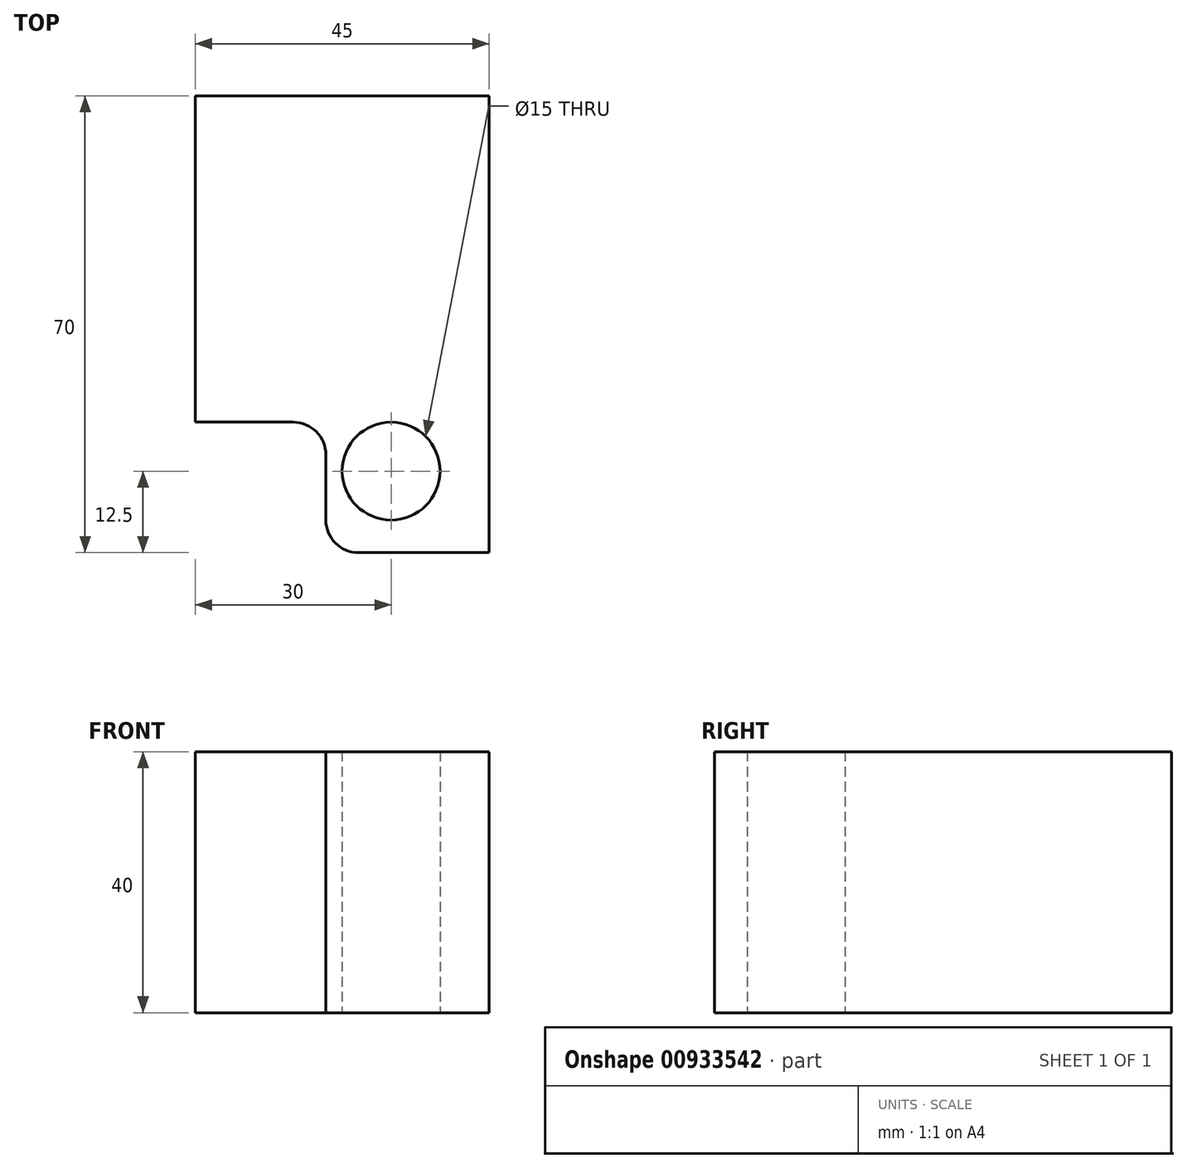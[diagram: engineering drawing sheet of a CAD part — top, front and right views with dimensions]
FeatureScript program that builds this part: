
annotation { "Feature Type Name" : "Feature", "Feature Type Description" : "" }
export const myFeature = defineFeature(function(context is Context, id is Id, definition is map)
    precondition{}
    {
        {
            var Q0;
            Q0=qCreatedBy(makeId("Top.planeOp"),FACE);
            var sketch = newSketch(context, id + "F0", { "sketchPlane" : qUnion([Q0])});
            skLineSegment(sketch, "E0.bottom", {"start": v(0, 0) * mm, "end": v(40, 0) * mm});
            skLineSegment(sketch, "E0.top", {"start": v(0, -5) * mm, "end": v(15, -5) * mm});
            skLineSegment(sketch, "E0.left", {"start": v(0, 0) * mm, "end": v(0, -5) * mm});
            skLineSegment(sketch, "E0.right", {"start": v(40, 0) * mm, "end": v(40, -5) * mm});
            skLineSegment(sketch, "E1", {"start": v(40, 0) * mm, "end": v(40, -12.5) * mm, "construction": true});
            skLineSegment(sketch, "E2", {"start": v(40, -12.5) * mm, "end": v(30, -12.5) * mm, "construction": true});
            skCircle(sketch, "E3", {"center": v(30, -12.5) * mm, "radius": 7.5 * mm});
            skLineSegment(sketch, "E4.top", {"start": v(35, -25) * mm, "end": v(25, -25) * mm});
            skLineSegment(sketch, "E4.right", {"start": v(20, -10) * mm, "end": v(20, -20) * mm});
            skPoint(sketch, "E5.visualSharp", {"position": v(40, -25) * mm});
            skPoint(sketch, "E6.visualSharp", {"position": v(20, -25) * mm});
            skArc(sketch, "E6.filletArc", {"start": v(20, -20) * mm, "mid": v(21.46, -23.54) * mm, "end": v(25, -25) * mm});
            skArc(sketch, "E7.filletArc", {"start": v(20, -10) * mm, "mid": v(18.54, -6.46) * mm, "end": v(15, -5) * mm});
            skLineSegment(sketch, "E8.bottom", {"start": v(40, 0) * mm, "end": v(45, 0) * mm});
            skLineSegment(sketch, "E8.right", {"start": v(45, 0) * mm, "end": v(45, -19.16) * mm});
            skLineSegment(sketch, "E9.bottom", {"start": v(0, 0) * mm, "end": v(45, 0) * mm});
            skLineSegment(sketch, "E9.top", {"start": v(0, 45) * mm, "end": v(45, 45) * mm});
            skLineSegment(sketch, "E9.left", {"start": v(0, 0) * mm, "end": v(0, 45) * mm});
            skLineSegment(sketch, "E9.right", {"start": v(45, 0) * mm, "end": v(45, 45) * mm});
            skLineSegment(sketch, "E10", {"start": v(35, -25) * mm, "end": v(45, -25) * mm});
            skLineSegment(sketch, "E11", {"start": v(45, -25) * mm, "end": v(45, -19.16) * mm});
            skLineSegment(sketch, "E12", {"start": v(30, -12.5) * mm, "end": v(45, -12.5) * mm, "construction": true});
            skSolve(sketch);
        }
        {
            var Q0;
            Q0=makeQuery(id+"F0.imprint","IMPRINT",FACE,{"disambiguationData":[TD([[makeQuery(id+"F0.imprint","IMPRINT",EDGE,{"derivedFrom":sQuery(id+"F0.wireOp",EDGE,"E0.bottom")}),-1.0]])]});
            var Q1;
            Q1=makeQuery(id+"F0.imprint","IMPRINT",FACE,{"disambiguationData":[TD([[makeQuery(id+"F0.imprint","IMPRINT",EDGE,{"derivedFrom":sQuery(id+"F0.wireOp",EDGE,"E0.bottom")}),1.0]])]});
            var Q2;
            Q2=makeQuery(id+"F0.imprint","IMPRINT",FACE,{"disambiguationData":[TD([[makeQuery(id+"F0.imprint","IMPRINT",EDGE,{"derivedFrom":sQuery(id+"F0.wireOp",EDGE,"E0.bottom")}),-1.0]])]});
            var Q3;
            {var subQ3=sQuery(id+"F0.wireOp",EDGE,"E8.top");Q3=makeQuery(id+"F0.imprint","IMPRINT",FACE,{"disambiguationData":[TD([[makeQuery(id+"F0.imprint","IMPRINT",EDGE,{"derivedFrom":subQ3}),1.0]])]});}
            extrude(context, id + "F1", {"entities" : qUnion([Q0, Q1, Q2, Q3]), "depth" : 40 * mm, "offsetDistance" : 25 * mm});
        }
    });
